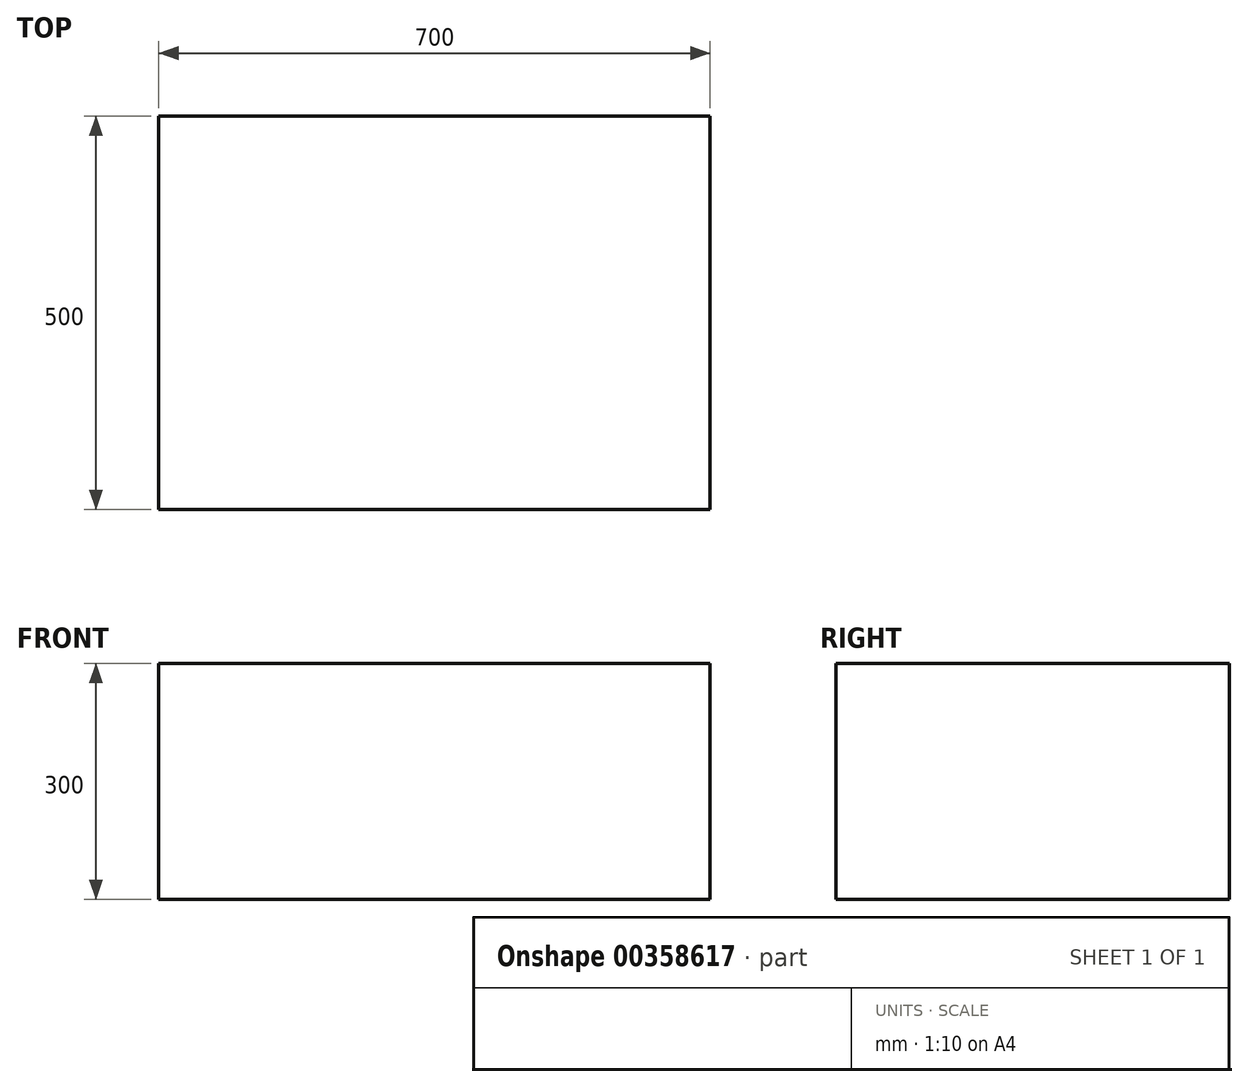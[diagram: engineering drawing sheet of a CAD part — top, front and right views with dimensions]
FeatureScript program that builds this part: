
annotation { "Feature Type Name" : "Feature", "Feature Type Description" : "" }
export const myFeature = defineFeature(function(context is Context, id is Id, definition is map)
    precondition{}
    {
        {
            var Q0;
            Q0=qCreatedBy(makeId("Top.planeOp"),FACE);
            var sketch = newSketch(context, id + "F0", { "sketchPlane" : qUnion([Q0])});
            skLineSegment(sketch, "E0.bottom", {"start": v(-350, 250) * mm, "end": v(350, 250) * mm});
            skLineSegment(sketch, "E0.top", {"start": v(-350, -250) * mm, "end": v(350, -250) * mm});
            skLineSegment(sketch, "E0.left", {"start": v(-350, 250) * mm, "end": v(-350, -250) * mm});
            skLineSegment(sketch, "E0.right", {"start": v(350, 250) * mm, "end": v(350, -250) * mm});
            skPoint(sketch, "E0.middle", {"position": v(0, 0) * mm});
            skSolve(sketch);
        }
        {
            var Q0;
            Q0 = qSketchRegion(id + "F0", true);
            extrude(context, id + "F1", {"entities" : qUnion([Q0]), "depth" : 300 * mm});
        }
    });
